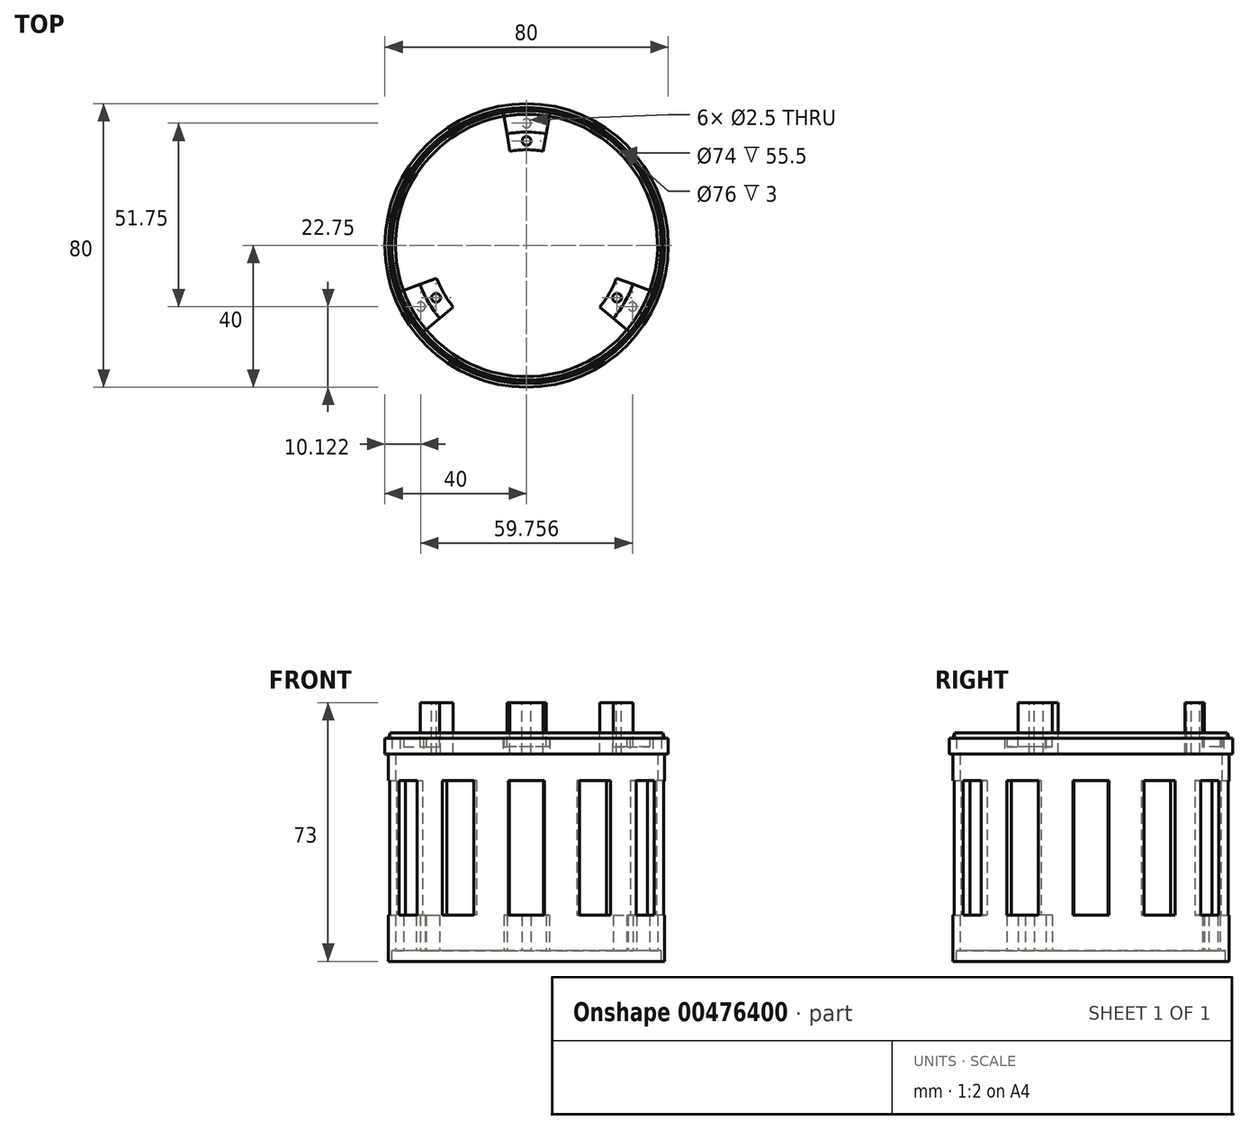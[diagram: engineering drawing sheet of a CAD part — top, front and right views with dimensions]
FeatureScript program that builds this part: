
annotation { "Feature Type Name" : "Feature", "Feature Type Description" : "" }
export const myFeature = defineFeature(function(context is Context, id is Id, definition is map)
    precondition{}
    {
        {
            var Q0;
            Q0=qCreatedBy(makeId("Top.planeOp"),FACE);
            var sketch = newSketch(context, id + "F0", { "sketchPlane" : qUnion([Q0])});
            skCircle(sketch, "E0", {"center": v(0, 0) * mm, "radius": 39 * mm});
            skSolve(sketch);
        }
        {
            var Q0;
            Q0=makeQuery(id+"F0.imprint","IMPRINT",FACE,{"disambiguationData":[TD([[makeQuery(id+"F0.imprint","IMPRINT",EDGE,{"derivedFrom":sQuery(id+"F0.wireOp",EDGE,"E0")}),1.0]])]});
            extrude(context, id + "F1", {"entities" : qUnion([Q0]), "depth" : 3 * mm});
        }
        {
            var Q0;
            Q0=makeQuery(id+"F1.opExtrude","CAP_FACE",FACE,{"disambiguationData":[OSD([sQuery(id+"F0.wireOp",EDGE,"E0")])],"isStart":false});
            var sketch = newSketch(context, id + "F2", { "sketchPlane" : qUnion([Q0])});
            skCircle(sketch, "E1", {"center": v(0, 0) * mm, "radius": 39 * mm});
            skCircle(sketch, "E2", {"center": v(0, 0) * mm, "radius": 37 * mm});
            skSolve(sketch);
        }
        {
            var Q0;
            Q0=makeQuery(id+"F2.imprint","IMPRINT",FACE,{"disambiguationData":[TD([[makeQuery(id+"F2.imprint","IMPRINT",EDGE,{"derivedFrom":sQuery(id+"F2.wireOp",EDGE,"E1")}),1.0]])]});
            extrude(context, id + "F3", {"entities" : qUnion([Q0]), "operationType" : NewBodyOperationType.ADD, "depth" : 60 * mm});
        }
        {
            var Q0;
            Q0=qCreatedBy(makeId("Front.planeOp"),FACE);
            var sketch = newSketch(context, id + "F4", { "sketchPlane" : qUnion([Q0])});
            skLineSegment(sketch, "E3", {"start": v(-37, 60.5) * mm, "end": v(-32, 60.5) * mm});
            skLineSegment(sketch, "E4", {"start": v(-32, 60.5) * mm, "end": v(-32, 73) * mm});
            skLineSegment(sketch, "E5", {"start": v(-40, 63) * mm, "end": v(-39, 63) * mm});
            skLineSegment(sketch, "E6", {"start": v(-39, 63) * mm, "end": v(-38.5, 64.5) * mm});
            skLineSegment(sketch, "E7", {"start": v(-38.5, 64.5) * mm, "end": v(-38, 63) * mm});
            skLineSegment(sketch, "E8", {"start": v(-38.5, 64.5) * mm, "end": v(-38.5, 63) * mm, "construction": true});
            skLineSegment(sketch, "E9", {"start": v(-40, 63) * mm, "end": v(-40, 58.5) * mm});
            skLineSegment(sketch, "E10", {"start": v(-40, 58.5) * mm, "end": v(-27, 58.5) * mm});
            skLineSegment(sketch, "E11", {"start": v(-27, 58.5) * mm, "end": v(-27, 73) * mm});
            skLineSegment(sketch, "E12", {"start": v(-27, 73) * mm, "end": v(-32, 73) * mm});
            skLineSegment(sketch, "E13", {"start": v(-39, 63) * mm, "end": v(-38.5, 63) * mm, "construction": true});
            skLineSegment(sketch, "E14", {"start": v(-38, 63) * mm, "end": v(-37, 63) * mm});
            skLineSegment(sketch, "E15", {"start": v(-37, 60.5) * mm, "end": v(-37, 63) * mm});
            skSolve(sketch);
        }
        {
            var Q0;
            Q0=qSketchRegion(id+"F4",true);
            var Q1;
            Q1=makeQuery(id+"F3.opExtrude","CAP_EDGE",EDGE,{"disambiguationData":[OSD([sQuery(id+"F2.wireOp",EDGE,"E1")])],"isStart":false});
            sweep(context, id + "F5", {"operationType" : NewBodyOperationType.ADD, "profiles" : qUnion([Q0]), "path" : qUnion([Q1])});
        }
        {
            var Q0;
            Q0=makeQuery(id+"F5.opSweep","SWEPT_FACE",FACE,{"disambiguationData":[OSD([sQuery(id+"F2.wireOp",EDGE,"E1"),sQuery(id+"F4.wireOp",EDGE,"E10")])]});
            var sketch = newSketch(context, id + "F6", { "sketchPlane" : qUnion([Q0])});
            skArc(sketch, "E16", {"start": v(6.6, -37.42) * mm, "mid": v(32.9, -19) * mm, "end": v(35.7, 13) * mm});
            skArc(sketch, "E17", {"start": v(1.74, -9.85) * mm, "mid": v(8.66, -5) * mm, "end": v(9.4, 3.42) * mm});
            skLineSegment(sketch, "E18", {"start": v(0, 0) * mm, "end": v(1.74, -9.85) * mm, "construction": true});
            skLineSegment(sketch, "E19", {"start": v(1.74, -9.85) * mm, "end": v(6.6, -37.42) * mm});
            skLineSegment(sketch, "E20", {"start": v(0, 0) * mm, "end": v(-1.74, -9.85) * mm, "construction": true});
            skLineSegment(sketch, "E21", {"start": v(-1.74, -9.85) * mm, "end": v(-6.6, -37.42) * mm});
            skLineSegment(sketch, "E22", {"start": v(0, 0) * mm, "end": v(0, -38) * mm, "construction": true});
            skLineSegment(sketch, "E23", {"start": v(-6.6, -37.42) * mm, "end": v(0, -38) * mm, "construction": true});
            skLineSegment(sketch, "E24", {"start": v(6.6, -37.42) * mm, "end": v(0, -38) * mm, "construction": true});
            skLineSegment(sketch, "E25.1.0", {"start": v(7.66, 6.43) * mm, "end": v(29.1, 24.43) * mm});
            skLineSegment(sketch, "E25.1.1", {"start": v(9.4, 3.42) * mm, "end": v(35.7, 13) * mm});
            skLineSegment(sketch, "E25.2.0", {"start": v(-9.4, 3.42) * mm, "end": v(-35.7, 13) * mm});
            skLineSegment(sketch, "E25.2.1", {"start": v(-7.66, 6.43) * mm, "end": v(-29.1, 24.43) * mm});
            skArc(sketch, "E26.trimOffspring", {"start": v(-35.7, 13) * mm, "mid": v(-32.9, -19) * mm, "end": v(-6.6, -37.42) * mm});
            skArc(sketch, "E27.trimOffspring", {"start": v(-9.4, 3.42) * mm, "mid": v(-8.66, -5) * mm, "end": v(-1.74, -9.85) * mm});
            skArc(sketch, "E28.trimOffspring", {"start": v(29.1, 24.43) * mm, "mid": v(0, 38) * mm, "end": v(-29.1, 24.43) * mm});
            skArc(sketch, "E29.trimOffspring", {"start": v(7.66, 6.43) * mm, "mid": v(0, 10) * mm, "end": v(-7.66, 6.43) * mm});
            skSolve(sketch);
        }
        {
            var Q0;
            Q0=qSketchRegion(id+"F6",true);
            var Q1;
            Q1=makeQuery(id+"F5.opSweep","SWEPT_FACE",FACE,{"disambiguationData":[OSD([sQuery(id+"F2.wireOp",EDGE,"E1"),sQuery(id+"F4.wireOp",EDGE,"E12")])]});
            extrude(context, id + "F7", {"entities" : qUnion([Q0]), "operationType" : NewBodyOperationType.REMOVE, "endBound" : BoundingType.UP_TO_SURFACE, "oppositeDirection" : true, "endBoundEntityFace" : qUnion([Q1]), "depth" : 25 * mm});
        }
        {
            var Q0;
            {var subQ0=sQuery(id+"F2.wireOp",EDGE,"E1");Q0=makeQuery(id+"F7.boolean.opBoolean","SPLIT",FACE,{"disambiguationData":[TD([makeQuery(id+"F7.opExtrude","SWEPT_FACE",FACE,{"disambiguationData":[OSD([sQuery(id+"F6.wireOp",EDGE,"E25.2.0")])]})])],"derivedFrom":makeQuery(id+"F5.opSweep","SWEPT_FACE",FACE,{"disambiguationData":[OSD([subQ0,sQuery(id+"F4.wireOp",EDGE,"E12")])]})});}
            var sketch = newSketch(context, id + "F8", { "sketchPlane" : qUnion([Q0])});
            skCircle(sketch, "E30", {"center": v(0, 29.5) * mm, "radius": 1.25 * mm});
            skLineSegment(sketch, "E31", {"start": v(0, 32) * mm, "end": v(0, 29.5) * mm, "construction": true});
            skLineSegment(sketch, "E32", {"start": v(0, 27) * mm, "end": v(0, 29.5) * mm, "construction": true});
            skCircle(sketch, "E33.1.0", {"center": v(-25.55, -14.75) * mm, "radius": 1.25 * mm});
            skCircle(sketch, "E33.2.0", {"center": v(25.55, -14.75) * mm, "radius": 1.25 * mm});
            skPoint(sketch, "E33.center", {"position": v(0, 0) * mm});
            skSolve(sketch);
        }
        {
            var Q0;
            Q0=qSketchRegion(id+"F8",true);
            extrude(context, id + "F9", {"entities" : qUnion([Q0]), "operationType" : NewBodyOperationType.REMOVE, "endBound" : BoundingType.UP_TO_NEXT, "oppositeDirection" : true, "depth" : 25 * mm});
        }
        {
            var Q0;
            Q0=makeQuery(id+"F1.opExtrude","CAP_FACE",FACE,{"disambiguationData":[OSD([sQuery(id+"F0.wireOp",EDGE,"E0")])],"isStart":false});
            var sketch = newSketch(context, id + "F10", { "sketchPlane" : qUnion([Q0])});
            skLineSegment(sketch, "E34", {"start": v(-6.42, 36.44) * mm, "end": v(-5.56, 31.51) * mm});
            skLineSegment(sketch, "E35", {"start": v(5.56, 31.51) * mm, "end": v(6.42, 36.44) * mm});
            skArc(sketch, "E36", {"start": v(6.42, 36.44) * mm, "mid": v(0, 37) * mm, "end": v(-6.42, 36.44) * mm});
            skLineSegment(sketch, "E37", {"start": v(-5.56, 31.51) * mm, "end": v(0, 0) * mm, "construction": true});
            skLineSegment(sketch, "E38", {"start": v(5.56, 31.51) * mm, "end": v(0, 0) * mm, "construction": true});
            skArc(sketch, "E39", {"start": v(5.56, 31.51) * mm, "mid": v(0, 32) * mm, "end": v(-5.56, 31.51) * mm});
            skLineSegment(sketch, "E40", {"start": v(0, 0) * mm, "end": v(0, 32) * mm, "construction": true});
            skLineSegment(sketch, "E41", {"start": v(0, 32) * mm, "end": v(0, 34.5) * mm, "construction": true});
            skLineSegment(sketch, "E42", {"start": v(0, 34.5) * mm, "end": v(0, 37) * mm, "construction": true});
            skCircle(sketch, "E43", {"center": v(0, 34.5) * mm, "radius": 1.25 * mm});
            skArc(sketch, "E44.1.0", {"start": v(-30.07, -10.94) * mm, "mid": v(-27.71, -16) * mm, "end": v(-24.51, -20.57) * mm});
            skCircle(sketch, "E44.1.1", {"center": v(-29.88, -17.25) * mm, "radius": 1.25 * mm});
            skLineSegment(sketch, "E44.1.2", {"start": v(-28.34, -23.78) * mm, "end": v(-24.51, -20.57) * mm});
            skArc(sketch, "E44.1.3", {"start": v(-34.77, -12.65) * mm, "mid": v(-32.04, -18.5) * mm, "end": v(-28.34, -23.78) * mm});
            skLineSegment(sketch, "E44.1.4", {"start": v(-30.07, -10.94) * mm, "end": v(-34.77, -12.65) * mm});
            skArc(sketch, "E44.2.0", {"start": v(24.51, -20.57) * mm, "mid": v(27.71, -16) * mm, "end": v(30.07, -10.94) * mm});
            skCircle(sketch, "E44.2.1", {"center": v(29.88, -17.25) * mm, "radius": 1.25 * mm});
            skLineSegment(sketch, "E44.2.2", {"start": v(34.77, -12.65) * mm, "end": v(30.07, -10.94) * mm});
            skArc(sketch, "E44.2.3", {"start": v(28.34, -23.78) * mm, "mid": v(32.04, -18.5) * mm, "end": v(34.77, -12.65) * mm});
            skLineSegment(sketch, "E44.2.4", {"start": v(24.51, -20.57) * mm, "end": v(28.34, -23.78) * mm});
            skSolve(sketch);
        }
        {
            var Q0;
            Q0=qSketchRegion(id+"F10",true);
            extrude(context, id + "F11", {"entities" : qUnion([Q0]), "operationType" : NewBodyOperationType.ADD, "depth" : 10 * mm});
        }
        {
            var Q0;
            Q0=makeQuery(id+"F11.boolean.opBoolean","SPLIT",FACE,{"disambiguationData":[TD([makeQuery(id+"F3.opExtrude","SWEPT_FACE",FACE,{"disambiguationData":[OSD([sQuery(id+"F2.wireOp",EDGE,"E2")])]})])],"derivedFrom":makeQuery(id+"F1.opExtrude","CAP_FACE",FACE,{"disambiguationData":[OSD([sQuery(id+"F0.wireOp",EDGE,"E0")])],"isStart":false})});
            var sketch = newSketch(context, id + "F12", { "sketchPlane" : qUnion([Q0])});
            skCircle(sketch, "E45", {"center": v(0, 0) * mm, "radius": 38 * mm});
            skSolve(sketch);
        }
        {
            var Q0;
            Q0=qSketchRegion(id+"F12",true);
            extrude(context, id + "F13", {"entities" : qUnion([Q0]), "operationType" : NewBodyOperationType.REMOVE, "endBound" : BoundingType.UP_TO_NEXT, "oppositeDirection" : true, "depth" : 25 * mm});
        }
        {
            var Q0;
            Q0=makeQuery(id+"F11.opExtrude","CAP_FACE",FACE,{"disambiguationData":[OSD([sQuery(id+"F10.wireOp",EDGE,"E34"),sQuery(id+"F10.wireOp",EDGE,"E35"),sQuery(id+"F10.wireOp",EDGE,"E36"),sQuery(id+"F10.wireOp",EDGE,"E39"),sQuery(id+"F10.wireOp",EDGE,"E43")])],"isStart":false});
            var sketch = newSketch(context, id + "F14", { "sketchPlane" : qUnion([Q0])});
            skLineSegment(sketch, "E46", {"start": v(0, 0) * mm, "end": v(4.57, 34.7) * mm, "construction": true});
            skLineSegment(sketch, "E47", {"start": v(4.57, 34.7) * mm, "end": v(5.87, 44.62) * mm});
            skLineSegment(sketch, "E48", {"start": v(5.87, 44.62) * mm, "end": v(-5.87, 44.62) * mm});
            skLineSegment(sketch, "E49", {"start": v(-5.87, 44.62) * mm, "end": v(-4.57, 34.7) * mm});
            skLineSegment(sketch, "E50", {"start": v(-4.57, 34.7) * mm, "end": v(0, 0) * mm, "construction": true});
            skLineSegment(sketch, "E51", {"start": v(4.57, 34.7) * mm, "end": v(-4.57, 34.7) * mm});
            skPoint(sketch, "E52.center", {"position": v(0, 0) * mm});
            skLineSegment(sketch, "E53", {"start": v(0, 0) * mm, "end": v(0, 34.7) * mm, "construction": true});
            skLineSegment(sketch, "E54.1.0", {"start": v(-27.4, 35.7) * mm, "end": v(-21.3, 27.77) * mm});
            skLineSegment(sketch, "E54.1.1", {"start": v(-17.22, 41.57) * mm, "end": v(-27.4, 35.7) * mm});
            skLineSegment(sketch, "E54.1.2", {"start": v(-13.4, 32.34) * mm, "end": v(-17.22, 41.57) * mm});
            skLineSegment(sketch, "E54.1.3", {"start": v(-13.4, 32.34) * mm, "end": v(-21.3, 27.77) * mm});
            skLineSegment(sketch, "E54.2.0", {"start": v(-41.57, 17.22) * mm, "end": v(-32.34, 13.4) * mm});
            skLineSegment(sketch, "E54.2.1", {"start": v(-35.7, 27.4) * mm, "end": v(-41.57, 17.22) * mm});
            skLineSegment(sketch, "E54.2.2", {"start": v(-27.77, 21.3) * mm, "end": v(-35.7, 27.4) * mm});
            skLineSegment(sketch, "E54.2.3", {"start": v(-27.77, 21.3) * mm, "end": v(-32.34, 13.4) * mm});
            skLineSegment(sketch, "E54.3.0", {"start": v(-44.62, -5.87) * mm, "end": v(-34.7, -4.57) * mm});
            skLineSegment(sketch, "E54.3.1", {"start": v(-44.62, 5.87) * mm, "end": v(-44.62, -5.87) * mm});
            skLineSegment(sketch, "E54.3.2", {"start": v(-34.7, 4.57) * mm, "end": v(-44.62, 5.87) * mm});
            skLineSegment(sketch, "E54.3.3", {"start": v(-34.7, 4.57) * mm, "end": v(-34.7, -4.57) * mm});
            skLineSegment(sketch, "E54.4.0", {"start": v(-35.7, -27.4) * mm, "end": v(-27.77, -21.3) * mm});
            skLineSegment(sketch, "E54.4.1", {"start": v(-41.57, -17.22) * mm, "end": v(-35.7, -27.4) * mm});
            skLineSegment(sketch, "E54.4.2", {"start": v(-32.34, -13.4) * mm, "end": v(-41.57, -17.22) * mm});
            skLineSegment(sketch, "E54.4.3", {"start": v(-32.34, -13.4) * mm, "end": v(-27.77, -21.3) * mm});
            skLineSegment(sketch, "E54.5.0", {"start": v(-17.22, -41.57) * mm, "end": v(-13.4, -32.34) * mm});
            skLineSegment(sketch, "E54.5.1", {"start": v(-27.4, -35.7) * mm, "end": v(-17.22, -41.57) * mm});
            skLineSegment(sketch, "E54.5.2", {"start": v(-21.3, -27.77) * mm, "end": v(-27.4, -35.7) * mm});
            skLineSegment(sketch, "E54.5.3", {"start": v(-21.3, -27.77) * mm, "end": v(-13.4, -32.34) * mm});
            skLineSegment(sketch, "E55.2.6.0", {"start": v(5.87, -44.62) * mm, "end": v(4.57, -34.7) * mm});
            skLineSegment(sketch, "E55.3.6.0", {"start": v(-5.87, -44.62) * mm, "end": v(5.87, -44.62) * mm});
            skLineSegment(sketch, "E55.6.6.0", {"start": v(-4.57, -34.7) * mm, "end": v(-5.87, -44.62) * mm});
            skLineSegment(sketch, "E55.9.6.0", {"start": v(-4.57, -34.7) * mm, "end": v(4.57, -34.7) * mm});
            skLineSegment(sketch, "E55.2.7.0", {"start": v(27.4, -35.7) * mm, "end": v(21.3, -27.77) * mm});
            skLineSegment(sketch, "E55.3.7.0", {"start": v(17.22, -41.57) * mm, "end": v(27.4, -35.7) * mm});
            skLineSegment(sketch, "E55.6.7.0", {"start": v(13.4, -32.34) * mm, "end": v(17.22, -41.57) * mm});
            skLineSegment(sketch, "E55.9.7.0", {"start": v(13.4, -32.34) * mm, "end": v(21.3, -27.77) * mm});
            skLineSegment(sketch, "E55.2.8.0", {"start": v(41.57, -17.22) * mm, "end": v(32.34, -13.4) * mm});
            skLineSegment(sketch, "E55.3.8.0", {"start": v(35.7, -27.4) * mm, "end": v(41.57, -17.22) * mm});
            skLineSegment(sketch, "E55.6.8.0", {"start": v(27.77, -21.3) * mm, "end": v(35.7, -27.4) * mm});
            skLineSegment(sketch, "E55.9.8.0", {"start": v(27.77, -21.3) * mm, "end": v(32.34, -13.4) * mm});
            skLineSegment(sketch, "E55.2.9.0", {"start": v(44.62, 5.87) * mm, "end": v(34.7, 4.57) * mm});
            skLineSegment(sketch, "E55.3.9.0", {"start": v(44.62, -5.87) * mm, "end": v(44.62, 5.87) * mm});
            skLineSegment(sketch, "E55.6.9.0", {"start": v(34.7, -4.57) * mm, "end": v(44.62, -5.87) * mm});
            skLineSegment(sketch, "E55.9.9.0", {"start": v(34.7, -4.57) * mm, "end": v(34.7, 4.57) * mm});
            skLineSegment(sketch, "E55.2.10.0", {"start": v(35.7, 27.4) * mm, "end": v(27.77, 21.3) * mm});
            skLineSegment(sketch, "E55.3.10.0", {"start": v(41.57, 17.22) * mm, "end": v(35.7, 27.4) * mm});
            skLineSegment(sketch, "E55.6.10.0", {"start": v(32.34, 13.4) * mm, "end": v(41.57, 17.22) * mm});
            skLineSegment(sketch, "E55.9.10.0", {"start": v(32.34, 13.4) * mm, "end": v(27.77, 21.3) * mm});
            skLineSegment(sketch, "E55.2.11.0", {"start": v(17.22, 41.57) * mm, "end": v(13.4, 32.34) * mm});
            skLineSegment(sketch, "E55.3.11.0", {"start": v(27.4, 35.7) * mm, "end": v(17.22, 41.57) * mm});
            skLineSegment(sketch, "E55.6.11.0", {"start": v(21.3, 27.77) * mm, "end": v(27.4, 35.7) * mm});
            skLineSegment(sketch, "E55.9.11.0", {"start": v(21.3, 27.77) * mm, "end": v(13.4, 32.34) * mm});
            skSolve(sketch);
        }
        {
            var Q0;
            Q0=qSketchRegion(id+"F14",true);
            var Q1;
            {var subQ0=sQuery(id+"F2.wireOp",EDGE,"E1");var subQ2=sQuery(id+"F6.wireOp",EDGE,"E25.1.0");Q1=makeQuery(id+"F7.boolean.opBoolean","SPLIT",FACE,{"disambiguationData":[TD([makeQuery(id+"F7.opExtrude","SWEPT_FACE",FACE,{"disambiguationData":[OSD([subQ2])]})])],"derivedFrom":makeQuery(id+"F5.opSweep","SWEPT_FACE",FACE,{"disambiguationData":[OSD([subQ0,sQuery(id+"F4.wireOp",EDGE,"E10")])]})});}
            extrude(context, id + "F15", {"entities" : qUnion([Q0]), "operationType" : NewBodyOperationType.REMOVE, "endBoundEntity" : qUnion([Q1]), "depth" : 38 * mm});
        }
    });
